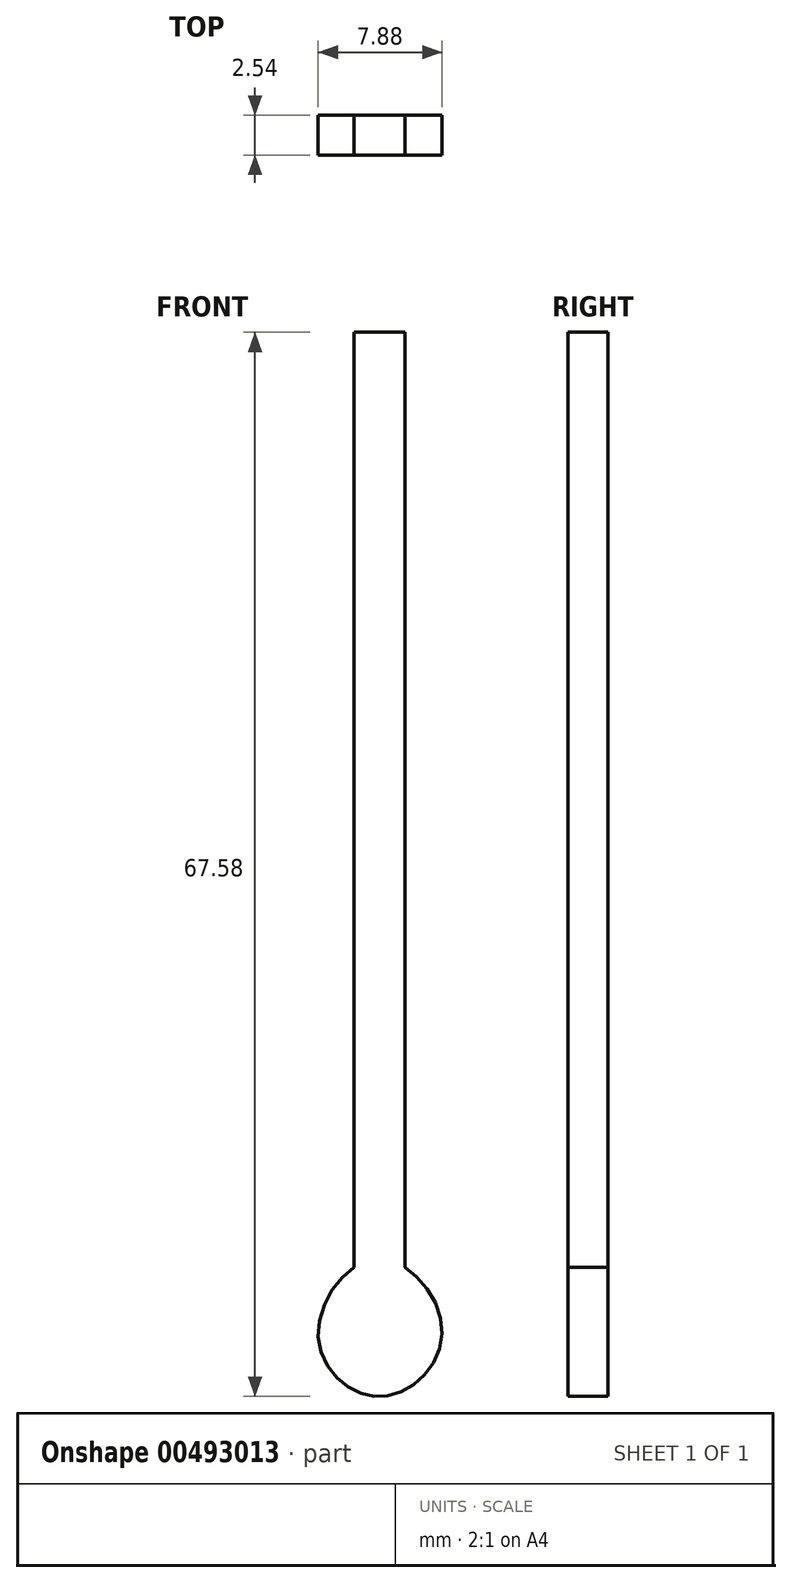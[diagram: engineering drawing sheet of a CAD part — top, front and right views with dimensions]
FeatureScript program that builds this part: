
annotation { "Feature Type Name" : "Feature", "Feature Type Description" : "" }
export const myFeature = defineFeature(function(context is Context, id is Id, definition is map)
    precondition{}
    {
        {
            var Q0;
            Q0=qCreatedBy(makeId("Front.planeOp"),FACE);
            var sketch = newSketch(context, id + "F0", { "sketchPlane" : qUnion([Q0])});
            skLineSegment(sketch, "E0", {"start": v(-29.47, 44.55) * mm, "end": v(-29.47, -14.85) * mm});
            skLineSegment(sketch, "E1", {"start": v(-26.24, 44.55) * mm, "end": v(-26.24, -14.85) * mm});
            skFitSpline(sketch, "E2", {"points": [v(-29.47, -14.85) * mm, v(-31.74, -19.16) * mm, v(-29.47, -22.65) * mm, v(-25.98, -22.5) * mm, v(-23.86, -18.86) * mm, v(-26.24, -14.85) * mm, v(-29.47, -14.85) * mm]});
            skLineSegment(sketch, "E3", {"start": v(-29.47, 44.55) * mm, "end": v(-26.24, 44.55) * mm});
            skSolve(sketch);
        }
        {
            var Q0;
            Q0 = qSketchRegion(id + "F0", true);
            extrude(context, id + "F1", {"entities" : qUnion([Q0]), "depth" : 2.54 * mm});
        }
    });
